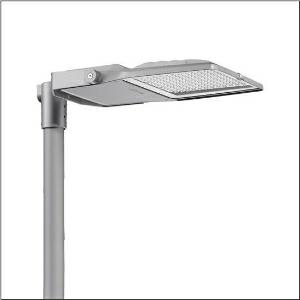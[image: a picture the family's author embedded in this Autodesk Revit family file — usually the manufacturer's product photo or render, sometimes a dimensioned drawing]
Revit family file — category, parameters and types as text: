
# Revit family: floodlight_fl_21_iq_midi___pl43_5xa7782e2a3a_72be
name_source: partatom
category: Lighting Fixtures
units: mm (PartAtom-declared; Revit-internal decimal feet)

## family parameters
Cut with Voids When Loaded = No
Host = Face
Light Source = No
Part Type = Normal
Room Calculation Point = No
Round Connector Dimension = Use Diameter
Shared = No

## types (1)
- --- (1 x LED, 27540 lm, 208.1 W, 3000K)
    Apparent Load = 208 VA
    CIE Flux Codes = 27 78 99 100 100
    Color Rendering = 70
    Color Temperature = 3000K
    Default Elevation = 1800 mm
    Description = Floodlight FL 21 iQ midi, floodlight, primary light control with lens, of PMMA, primary optical cover: protective disc, of toughened safety glass, transparent, light distribution: PL43, light emission: direct distribution, installation type: surface-mounted, lamps: LED, High Power LED, rated values: 27.540lm | 208,1W | 132,3lm/W (begin service life); end service life: 27.540lm | 227,1W; at 50% lumin. flux: 13.770lm | 90,1W | 152,8lm/W, colour temperature: 3000K, colour rendering: CRI > 70, light colour: 730, light setting 1 begin service life: 100% | 27.540lm | 208,1W | 132,3lm/W | 3.000K, light setting 1 end service life: 227,1W, further light settings possible, control: optimised constant luminous flux control (CLO 2.0), Desk-Remote (wireless, voltage-free reading and setting of iQ features in the workshop via application-optimized NFC function/RFID function), Smart-Wire, Night-Set, Temp-Guard, Auto-Match, Street-Remote, pre-setting: linear dimming characteristic, with terminal, 6-pole, mains connection: 220..240V, AC, 50/60Hz, luminaire housing, of diecast aluminium, powder-coated, SITECO metallic grey (DB 702S), corrosivity category C5 mid according to DIN EN ISO 12944suitable for swimming poolschlorine-resistant, sealing non-destructively replaceable, please order mast flange separately, mast bracket, of steel, galvanised, powder-coated, SITECO metallic grey (DB 702S), protection rating (complete): IP66, insulation class (complete): insulation class II (safety insulation), certification: CE, ENEC, VDE, protection symbol: D, impact resistance: IK08, permissible operating ambient temperature: -40..+40°C, permissible operating ambient temperature for outdoor applications: -40..+50°C, standard: DIN EN 12944, LABS conformity tested according to VDMA 24364:2018-05, packaging unit: 1 piece

Light Distribution: PL43
    Height = 76 mm
    Lamp = 1 x LED
    Lamp Light Flux = 27540 lm
    Lamp Power = 208.1 W
    Lamp count = 1
    Length = 657 mm
    Luminous efficacy = 132 lm/W
    Manufacturer = Siteco
    ModVariant = No
    Model = 5XA7782E2A3A
    Number of Poles = 1
    OnlyDefault = Yes
    Power Factor = 1
    Product Name = Floodlight FL 21 iQ midi | PL43
    Product group = floodlight | pylon annexe
    ProductGroupID = 6201
    Protection Class = Protection class II
    Protection Degree = IP 66
    RLX_Detail_Level = 1
    RLX_Emergency_Light_Flux = 0 lm
    RLX_Emergency_Type = 0
    RLX_Emergency_Type_DB = No
    RlxData = <blob elided: 153905 chars, md5=993b7265>
    Socket = socket
    Standby Power = 0 W
    System Light Flux = 27540 lm
    System Power = 208 W
    Type Comments = factory setting: luminous flux: 100 % | dim-lin: 254 | 710 mA
    Type Image = l_1007123.jpg
    URL = http://relux.com
    VarID = @adj_105131
    Voltage = 0 V
    Weight = 0.00 kg
    Width = 442 mm

## geometry (parser evidence)
native form markers: Blend x4, Sweep x12
no freeform markers — native parametric forms only
